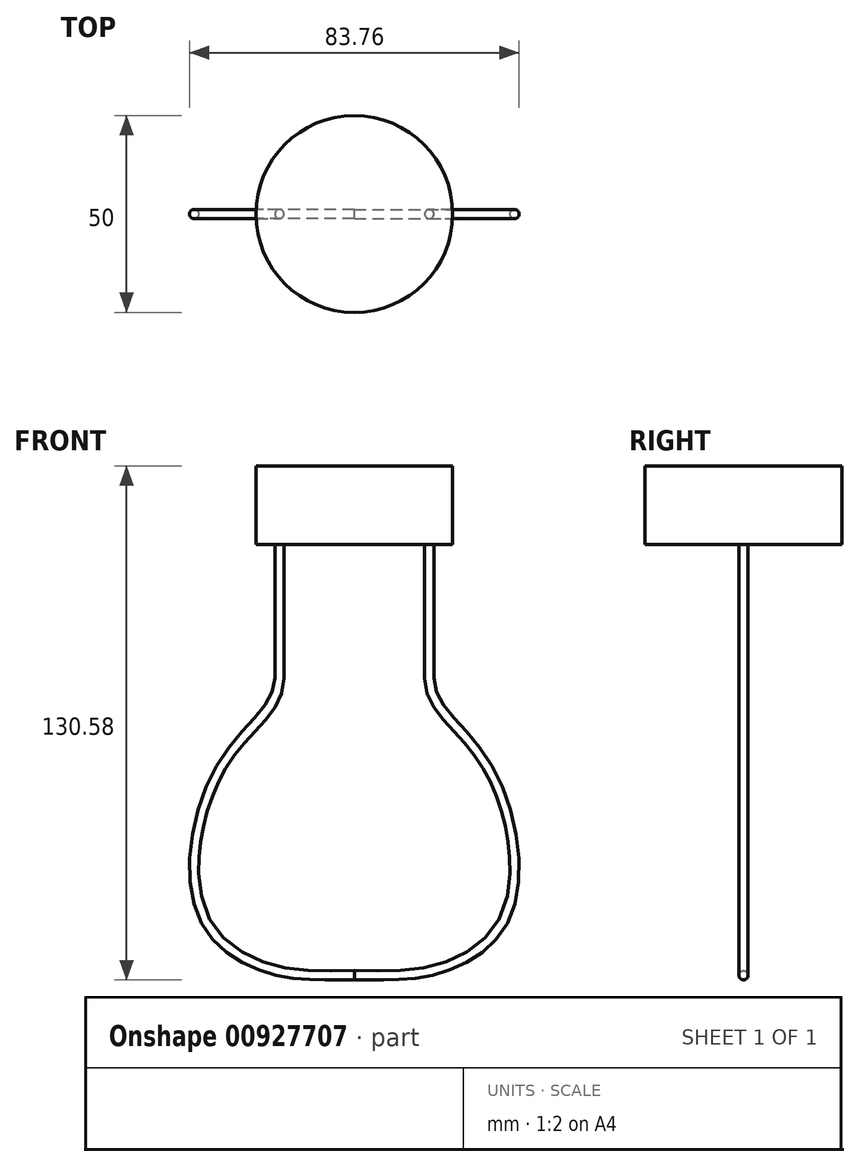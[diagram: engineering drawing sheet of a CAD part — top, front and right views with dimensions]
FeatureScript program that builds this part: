
annotation { "Feature Type Name" : "Feature", "Feature Type Description" : "" }
export const myFeature = defineFeature(function(context is Context, id is Id, definition is map)
    precondition{}
    {
        {
            var Q0;
            Q0=qCreatedBy(makeId("Front.planeOp"),FACE);
            var sketch = newSketch(context, id + "F0", { "sketchPlane" : qUnion([Q0])});
            skLineSegment(sketch, "E0", {"start": v(19.14, 82.37) * mm, "end": v(19.14, 47.1) * mm});
            skFitSpline(sketch, "E1", {"points": [v(19.14, 47.1) * mm, v(32.75, 26.45) * mm, v(38.8, -12.85) * mm, v(19.14, -27.46) * mm, v(0, -28.47) * mm], "startDerivative": vector(0, -97.82) * mm, "endDerivative": vector(-81.82, -0.99) * mm});
            skLineSegment(sketch, "E2", {"start": v(0, 75.73) * mm, "end": v(0, -75.73) * mm, "construction": true});
            skFitSpline(sketch, "E3.MirrorCS", {"points": [v(-19.14, 47.1) * mm, v(-32.75, 26.45) * mm, v(-38.8, -12.85) * mm, v(-19.14, -27.46) * mm, v(0, -28.47) * mm], "startDerivative": vector(0, -97.82) * mm, "endDerivative": vector(81.82, -0.99) * mm});
            skLineSegment(sketch, "E4.MirrorCS", {"start": v(-19.14, 82.37) * mm, "end": v(-19.14, 47.1) * mm});
            skSolve(sketch);
        }
        {
            var Q0;
            Q0=qCreatedBy(makeId("Top.planeOp"),FACE);
            cPlane(context, id + "F1", {"entities" : qUnion([Q0]), "cplaneType" : CPlaneType.OFFSET, "offset" : 81 * mm, "width" : 150 * mm, "height" : 150 * mm});
        }
        {
            var Q0;
            Q0=qCreatedBy(id+"F1.planeOp",FACE);
            var sketch = newSketch(context, id + "F2", { "sketchPlane" : qUnion([Q0])});
            skCircle(sketch, "E5", {"center": v(19.04, 0) * mm, "radius": 1.16 * mm});
            skSolve(sketch);
        }
        {
            var Q0;
            Q0 = qSketchRegion(id + "F2", true);
            var Q1;
            Q1=sQuery(id+"F0.wireOp",EDGE,"E0");
            var Q2;
            Q2=sQuery(id+"F0.wireOp",EDGE,"E1");
            var Q3;
            Q3=sQuery(id+"F0.wireOp",EDGE,"E3.MirrorCS");
            var Q4;
            Q4=sQuery(id+"F0.wireOp",EDGE,"E4.MirrorCS");
            sweep(context, id + "F3", {"profiles" : qUnion([Q0]), "path" : qUnion([Q1, Q2, Q3, Q4])});
        }
        {
            var Q0;
            Q0=qCreatedBy(id+"F1.planeOp",FACE);
            var sketch = newSketch(context, id + "F4", { "sketchPlane" : qUnion([Q0])});
            skCircle(sketch, "E6", {"center": v(0, 0) * mm, "radius": 25 * mm});
            skSolve(sketch);
        }
        {
            var Q0;
            Q0=makeQuery(id+"F4.imprint","IMPRINT",FACE,{"disambiguationData":[TD([[makeQuery(id+"F4.imprint","IMPRINT",EDGE,{"derivedFrom":sQuery(id+"F4.wireOp",EDGE,"E6")}),1.0]])]});
            extrude(context, id + "F5", {"entities" : qUnion([Q0]), "operationType" : NewBodyOperationType.ADD, "depth" : 20 * mm, "offsetDistance" : 25 * mm});
        }
    });
